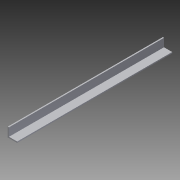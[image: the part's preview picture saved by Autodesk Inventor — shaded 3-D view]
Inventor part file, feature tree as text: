
AUTODESK INVENTOR PART (.ipt)
format: ipt  version: 2013 (Build 170138000, 138)  size: 73,728 bytes
history: native  units: in
note: dims shown in document units (in); Inventor stores cm internally (conversion verified against a paired STEP export)
features: extrude x1, sketch x1
ambient origin geometry x8: Origin, YZ Plane, XZ Plane, XY Plane, X Axis, Y Axis, Z Axis, Center Point
bodies: Solid1 (feature_tree)
feature tree (2):
  extrude  "Extrusion1"  Depth=0.0625in
  sketch  "Sketch1"  dims[d0=0.5in d1=0.0625in d2=0.5in d3=0.0625in d4=8.25in d5=0.0in]
